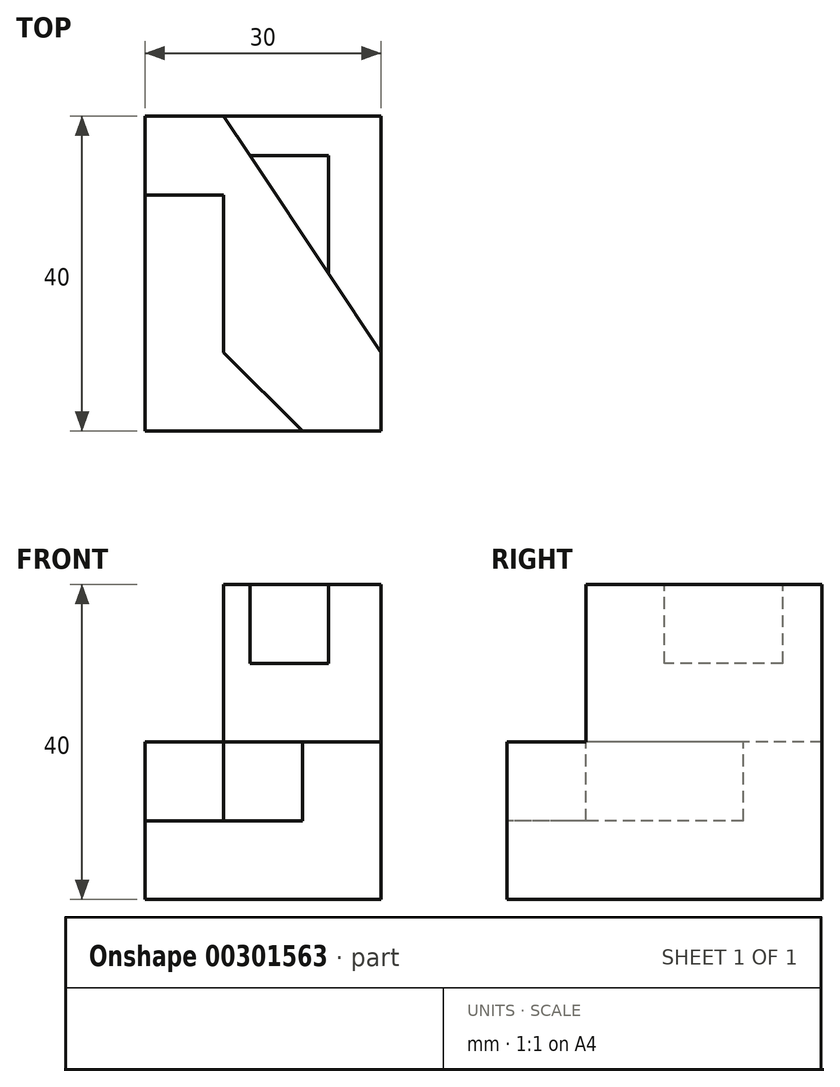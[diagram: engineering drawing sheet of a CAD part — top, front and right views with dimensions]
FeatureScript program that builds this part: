
annotation { "Feature Type Name" : "Feature", "Feature Type Description" : "" }
export const myFeature = defineFeature(function(context is Context, id is Id, definition is map)
    precondition{}
    {
        {
            var Q0;
            Q0=qCreatedBy(makeId("Top.planeOp"),FACE);
            var sketch = newSketch(context, id + "F0", { "sketchPlane" : qUnion([Q0])});
            skLineSegment(sketch, "E0.bottom", {"start": v(-20, 20) * mm, "end": v(20, 20) * mm});
            skLineSegment(sketch, "E0.top", {"start": v(-20, -20) * mm, "end": v(20, -20) * mm});
            skLineSegment(sketch, "E0.left", {"start": v(-20, 20) * mm, "end": v(-20, -20) * mm});
            skLineSegment(sketch, "E0.right", {"start": v(20, 20) * mm, "end": v(20, -20) * mm});
            skPoint(sketch, "E0.middle", {"position": v(0, 0) * mm});
            skSolve(sketch);
        }
        {
            var Q0;
            Q0=makeQuery(id+"F0.imprint","IMPRINT",FACE,{"disambiguationData":[TD([[makeQuery(id+"F0.imprint","IMPRINT",EDGE,{"derivedFrom":sQuery(id+"F0.wireOp",EDGE,"E0.bottom")}),-1.0]])]});
            extrude(context, id + "F1", {"entities" : qUnion([Q0]), "depth" : 30 * mm});
        }
        {
            var Q0;
            Q0=makeQuery(id+"F1.opExtrude","SWEPT_FACE",FACE,{"disambiguationData":[OSD([sQuery(id+"F0.wireOp",EDGE,"E0.right")])]});
            var sketch = newSketch(context, id + "F2", { "sketchPlane" : qUnion([Q0])});
            skLineSegment(sketch, "E1", {"start": v(-20, 30) * mm, "end": v(20, 30) * mm});
            skLineSegment(sketch, "E2", {"start": v(20, 30) * mm, "end": v(20, 20) * mm});
            skLineSegment(sketch, "E3", {"start": v(20, 20) * mm, "end": v(-10, 0) * mm});
            skLineSegment(sketch, "E4", {"start": v(-10, 0) * mm, "end": v(-20, 0) * mm});
            skLineSegment(sketch, "E5", {"start": v(-20, 0) * mm, "end": v(-20, 30) * mm});
            skSolve(sketch);
        }
        {
            var Q0;
            Q0=makeQuery(id+"F2.imprint","IMPRINT",FACE,{"disambiguationData":[TD([[makeQuery(id+"F2.imprint","IMPRINT",EDGE,{"derivedFrom":sQuery(id+"F2.wireOp",EDGE,"E1")}),1.0]])]});
            extrude(context, id + "F3", {"entities" : qUnion([Q0]), "operationType" : NewBodyOperationType.REMOVE, "oppositeDirection" : true, "depth" : 20 * mm});
        }
        {
            var Q0;
            Q0=makeQuery(id+"F3.boolean.opBoolean","COPY",FACE,{"derivedFrom":makeQuery(id+"F3.opExtrude","CAP_FACE",FACE,{"disambiguationData":[OSD([sQuery(id+"F2.wireOp",EDGE,"E1"),sQuery(id+"F2.wireOp",EDGE,"E2"),sQuery(id+"F2.wireOp",EDGE,"E3"),sQuery(id+"F2.wireOp",EDGE,"E4"),sQuery(id+"F2.wireOp",EDGE,"E5")])],"isStart":false})});
            var sketch = newSketch(context, id + "F4", { "sketchPlane" : qUnion([Q0])});
            skLineSegment(sketch, "E6", {"start": v(-20, 30) * mm, "end": v(10, 30) * mm});
            skLineSegment(sketch, "E7", {"start": v(10, 30) * mm, "end": v(10, 20) * mm});
            skLineSegment(sketch, "E8", {"start": v(10, 20) * mm, "end": v(-10, 20) * mm});
            skLineSegment(sketch, "E9", {"start": v(-10, 20) * mm, "end": v(-20, 10) * mm});
            skLineSegment(sketch, "E10", {"start": v(-20, 10) * mm, "end": v(-20, 30) * mm});
            skSolve(sketch);
        }
        {
            var Q0;
            Q0=makeQuery(id+"F4.imprint","IMPRINT",FACE,{"disambiguationData":[TD([[makeQuery(id+"F4.imprint","IMPRINT",EDGE,{"derivedFrom":sQuery(id+"F4.wireOp",EDGE,"E6")}),1.0]])]});
            extrude(context, id + "F5", {"entities" : qUnion([Q0]), "operationType" : NewBodyOperationType.REMOVE, "oppositeDirection" : true, "depth" : 10 * mm});
        }
        {
            var Q0;
            Q0=makeQuery(id+"F1.opExtrude","SWEPT_FACE",FACE,{"disambiguationData":[OSD([sQuery(id+"F0.wireOp",EDGE,"E0.right")])]});
            var sketch = newSketch(context, id + "F6", { "sketchPlane" : qUnion([Q0])});
            skLineSegment(sketch, "E11", {"start": v(15, 16.67) * mm, "end": v(15, 6.67) * mm});
            skLineSegment(sketch, "E12", {"start": v(15, 6.67) * mm, "end": v(0, 6.67) * mm});
            skLineSegment(sketch, "E13", {"start": v(0, 6.67) * mm, "end": v(15, 16.67) * mm});
            skSolve(sketch);
        }
        {
            var Q0;
            Q0=makeQuery(id+"F6.imprint","IMPRINT",FACE,{"disambiguationData":[TD([[makeQuery(id+"F6.imprint","IMPRINT",EDGE,{"derivedFrom":sQuery(id+"F6.wireOp",EDGE,"E11")}),-1.0]])]});
            extrude(context, id + "F7", {"entities" : qUnion([Q0]), "operationType" : NewBodyOperationType.REMOVE, "oppositeDirection" : true, "depth" : 10 * mm});
        }
        {
            var Q0;
            Q0=makeQuery(id+"F1.opExtrude","SWEPT_BODY",BODY,{"disambiguationData":[OSD([sQuery(id+"F0.wireOp",EDGE,"E0.bottom"),sQuery(id+"F0.wireOp",EDGE,"E0.top"),sQuery(id+"F0.wireOp",EDGE,"E0.left"),sQuery(id+"F0.wireOp",EDGE,"E0.right")])]});
            var Q1;
            Q1=makeQuery(id+"F1.opExtrude","CAP_EDGE",EDGE,{"disambiguationData":[OSD([sQuery(id+"F0.wireOp",EDGE,"E0.left")])],"isStart":true});
            transform(context, id + "F8", {"entities" : qUnion([Q0]), "transformType" : TransformType.ROTATION, "transformAxis" : qUnion([Q1]), "angle" : 90 * degree, "makeCopy" : false});
        }
        {
            var Q0;
            Q0=makeQuery(id+"F1.opExtrude","SWEPT_BODY",BODY,{"disambiguationData":[OSD([sQuery(id+"F0.wireOp",EDGE,"E0.bottom"),sQuery(id+"F0.wireOp",EDGE,"E0.top"),sQuery(id+"F0.wireOp",EDGE,"E0.left"),sQuery(id+"F0.wireOp",EDGE,"E0.right")])]});
            transform(context, id + "F9", {"entities" : qUnion([Q0]), "transformType" : TransformType.TRANSLATION_3D, "dx" : 33.4 * mm, "dy" : 0 * mm, "dz" : 0 * mm, "makeCopy" : false});
        }
    });
